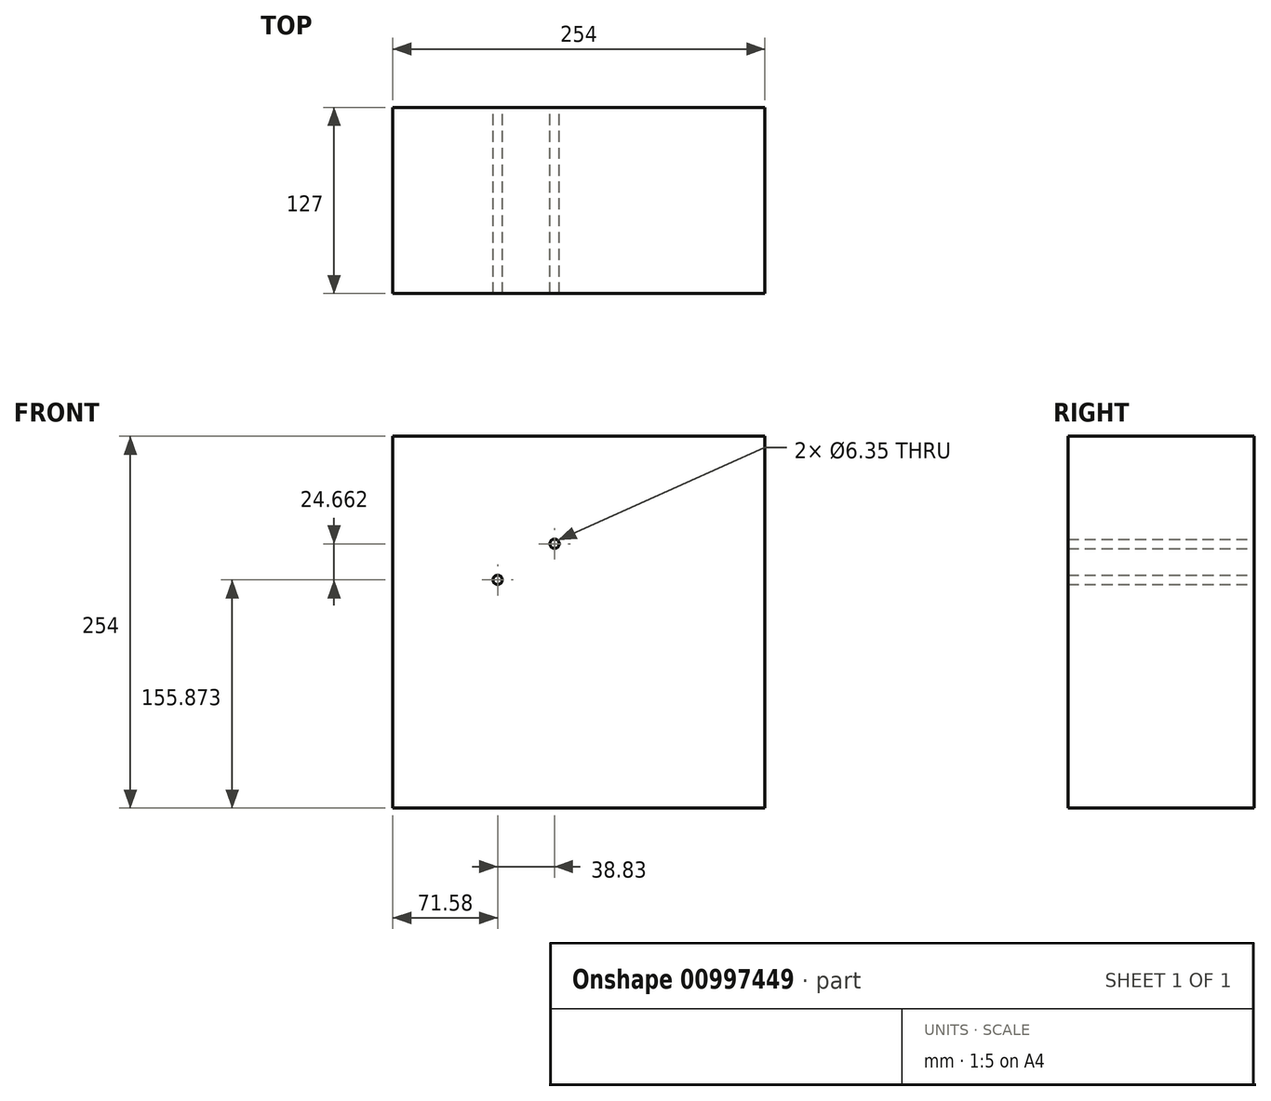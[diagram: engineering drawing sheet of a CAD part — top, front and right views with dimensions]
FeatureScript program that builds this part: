
annotation { "Feature Type Name" : "Feature", "Feature Type Description" : "" }
export const myFeature = defineFeature(function(context is Context, id is Id, definition is map)
    precondition{}
    {
        {
            var Q0;
            Q0=qCreatedBy(makeId("Front.planeOp"),FACE);
            var sketch = newSketch(context, id + "F0", { "sketchPlane" : qUnion([Q0])});
            skLineSegment(sketch, "E0.bottom", {"start": v(-127, 127) * mm, "end": v(127, 127) * mm});
            skLineSegment(sketch, "E0.top", {"start": v(-127, -127) * mm, "end": v(127, -127) * mm});
            skLineSegment(sketch, "E0.left", {"start": v(-127, 127) * mm, "end": v(-127, -127) * mm});
            skLineSegment(sketch, "E0.right", {"start": v(127, 127) * mm, "end": v(127, -127) * mm});
            skPoint(sketch, "E0.middle", {"position": v(0, 0) * mm});
            skCircle(sketch, "E1", {"center": v(-55.42, 28.87) * mm, "radius": 3.18 * mm});
            skCircle(sketch, "E2", {"center": v(-16.6, 53.54) * mm, "radius": 3.18 * mm});
            skSolve(sketch);
        }
        {
            var Q0;
            Q0 = qSketchRegion(id + "F0", true);
            extrude(context, id + "F1", {"entities" : qUnion([Q0]), "depth" : 127 * mm, "offsetDistance" : 25.4 * mm});
        }
    });
